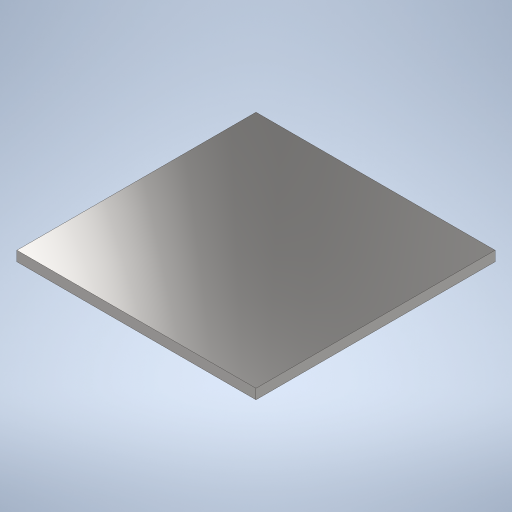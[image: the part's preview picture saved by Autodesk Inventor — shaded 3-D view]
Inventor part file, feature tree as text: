
AUTODESK INVENTOR PART (.ipt)
format: ipt  version: 2023.2 (Build 272271030, 271C)  size: 236,032 bytes
history: native  units: mm
features: other x1, extrude x1, sketch x1
ambient origin geometry x8: Origin, YZ Plane, XZ Plane, XY Plane, X Axis, Y Axis, Z Axis, Center Point
bodies: Body1 (feature_tree)
feature tree (3):
  other  "Sólido1"
  extrude  "Extrusão1"  Depth=120.0mm
  sketch  "Esboço1"  dims[d0=120.0mm d1=120.0mm d2=5.0mm d3=0.0mm]
